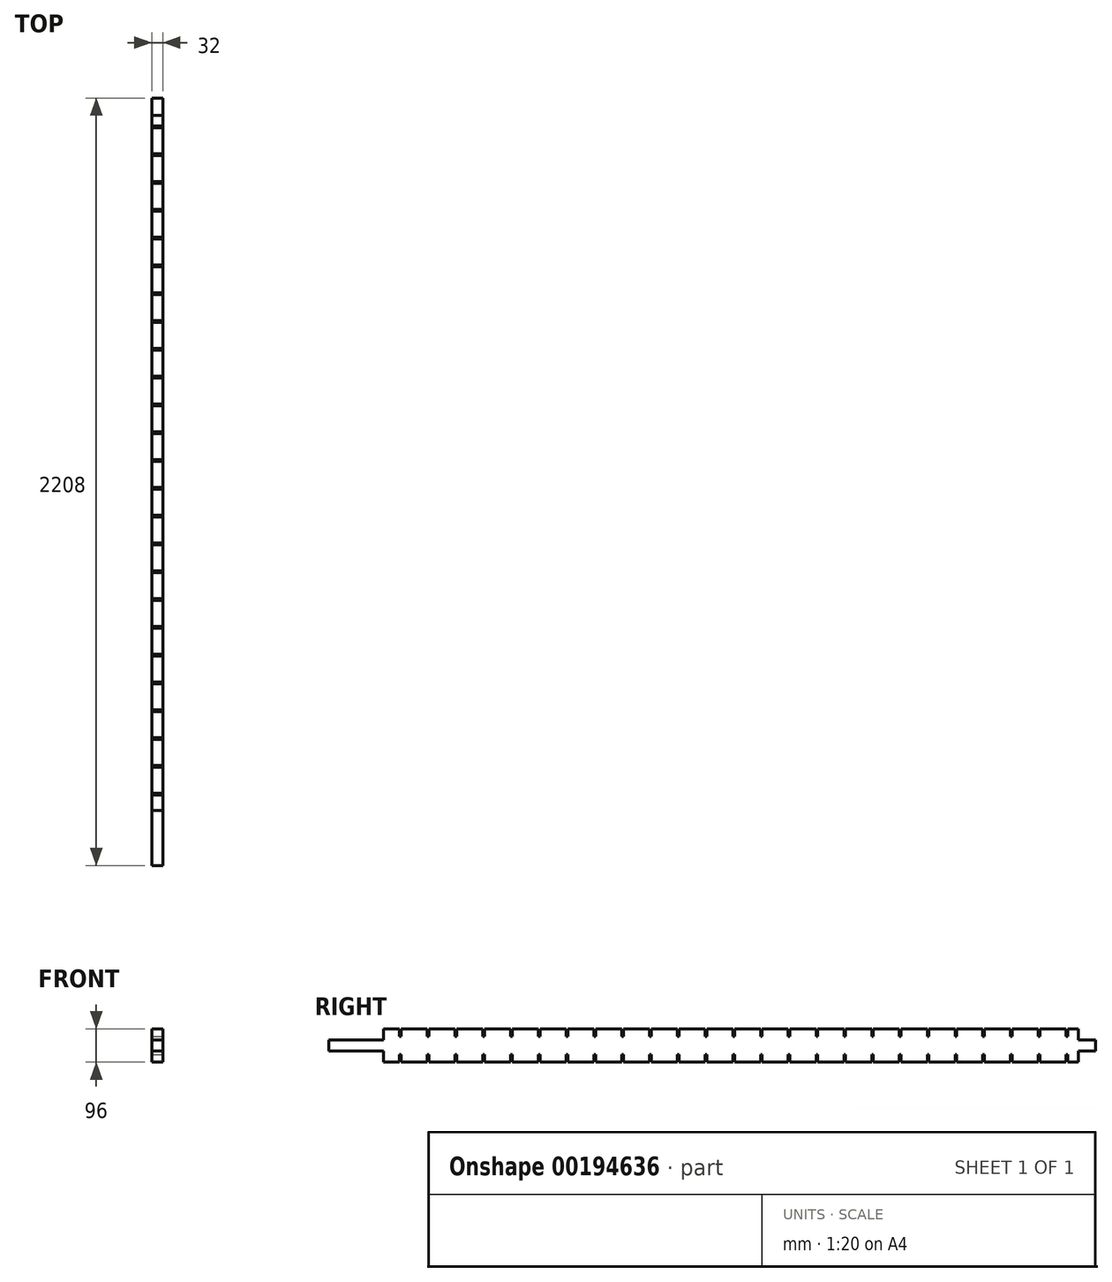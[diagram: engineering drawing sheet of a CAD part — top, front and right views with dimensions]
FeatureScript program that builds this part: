
annotation { "Feature Type Name" : "Feature", "Feature Type Description" : "" }
export const myFeature = defineFeature(function(context is Context, id is Id, definition is map)
    precondition{}
    {
        {
            var Q0;
            Q0=qCreatedBy(makeId("Front.planeOp"),FACE);
            var sketch = newSketch(context, id + "F0", { "sketchPlane" : qUnion([Q0])});
            skLineSegment(sketch, "E0.bottom", {"start": v(16, -16) * mm, "end": v(-16, -16) * mm});
            skLineSegment(sketch, "E0.top", {"start": v(16, 16) * mm, "end": v(-16, 16) * mm});
            skLineSegment(sketch, "E0.left", {"start": v(16, -16) * mm, "end": v(16, 16) * mm});
            skLineSegment(sketch, "E0.right", {"start": v(-16, -16) * mm, "end": v(-16, 16) * mm});
            skPoint(sketch, "E0.middle", {"position": v(0, 0) * mm});
            skSolve(sketch);
        }
        {
            var Q0;
            Q0 = qSketchRegion(id + "F0", true);
            extrude(context, id + "F1", {"entities" : qUnion([Q0]), "depth" : 2208 * mm});
        }
        {
            var Q0;
            Q0=qCreatedBy(makeId("Front.planeOp"),FACE);
            cPlane(context, id + "F2", {"entities" : qUnion([Q0]), "cplaneType" : CPlaneType.OFFSET, "offset" : 50 * mm, "width" : 150 * mm, "height" : 150 * mm});
        }
        {
            var Q0;
            Q0=qCreatedBy(id+"F2.planeOp",FACE);
            var sketch = newSketch(context, id + "F3", { "sketchPlane" : qUnion([Q0])});
            skLineSegment(sketch, "E1.bottom", {"start": v(16, 16) * mm, "end": v(-16, 16) * mm});
            skLineSegment(sketch, "E1.top", {"start": v(16, 48) * mm, "end": v(-16, 48) * mm});
            skLineSegment(sketch, "E1.left", {"start": v(16, 16) * mm, "end": v(16, 48) * mm});
            skLineSegment(sketch, "E1.right", {"start": v(-16, 16) * mm, "end": v(-16, 48) * mm});
            skPoint(sketch, "E1.middle", {"position": v(0, 32) * mm});
            skLineSegment(sketch, "E2.bottom", {"start": v(16, -16) * mm, "end": v(-16, -16) * mm});
            skLineSegment(sketch, "E2.top", {"start": v(16, -48) * mm, "end": v(-16, -48) * mm});
            skLineSegment(sketch, "E2.left", {"start": v(16, -16) * mm, "end": v(16, -48) * mm});
            skLineSegment(sketch, "E2.right", {"start": v(-16, -16) * mm, "end": v(-16, -48) * mm});
            skPoint(sketch, "E2.middle", {"position": v(0, -32) * mm});
            skSolve(sketch);
        }
        {
            var Q0;
            Q0 = qSketchRegion(id + "F3", true);
            extrude(context, id + "F4", {"entities" : qUnion([Q0]), "operationType" : NewBodyOperationType.ADD, "depth" : 2000 * mm});
        }
        {
            var Q0;
            Q0=makeQuery(id+"F4.boolean.opBoolean","MERGE",FACE,{"derivedFrom":[makeQuery(id+"F1.opExtrude","SWEPT_FACE",FACE,{"disambiguationData":[OSD([sQuery(id+"F0.wireOp",EDGE,"E0.left")])]}),makeQuery(id+"F4.opExtrude","SWEPT_FACE",FACE,{"disambiguationData":[OSD([sQuery(id+"F3.wireOp",EDGE,"E1.left")])]}),makeQuery(id+"F4.opExtrude","SWEPT_FACE",FACE,{"disambiguationData":[OSD([sQuery(id+"F3.wireOp",EDGE,"E2.left")])]})]});
            var sketch = newSketch(context, id + "F5", { "sketchPlane" : qUnion([Q0])});
            skLineSegment(sketch, "E3.0", {"start": v(-80, 26) * mm, "end": v(-80, 48) * mm});
            skLineSegment(sketch, "E4", {"start": v(-80, -48) * mm, "end": v(-85, -48) * mm});
            skLineSegment(sketch, "E5", {"start": v(-85, 48) * mm, "end": v(-85, 26) * mm});
            skLineSegment(sketch, "E6", {"start": v(-85, 26) * mm, "end": v(-80, 26) * mm});
            skLineSegment(sketch, "E7", {"start": v(-80, -26) * mm, "end": v(-80, -48) * mm});
            skLineSegment(sketch, "E8", {"start": v(-85, -26) * mm, "end": v(-80, -26) * mm});
            skLineSegment(sketch, "E9.trimOffspring", {"start": v(-85, -26) * mm, "end": v(-85, -48) * mm});
            skLineSegment(sketch, "E10", {"start": v(-85, 48) * mm, "end": v(-80, 48) * mm});
            skLineSegment(sketch, "E11.1.0.0", {"start": v(-160, 26) * mm, "end": v(-160, 48) * mm});
            skLineSegment(sketch, "E11.1.0.1", {"start": v(-165, 48) * mm, "end": v(-165, 26) * mm});
            skLineSegment(sketch, "E11.1.0.2", {"start": v(-165, 26) * mm, "end": v(-160, 26) * mm});
            skLineSegment(sketch, "E11.1.0.3", {"start": v(-160, -26) * mm, "end": v(-160, -48) * mm});
            skLineSegment(sketch, "E11.1.0.4", {"start": v(-165, -26) * mm, "end": v(-160, -26) * mm});
            skLineSegment(sketch, "E11.1.0.5", {"start": v(-165, -26) * mm, "end": v(-165, -48) * mm});
            skLineSegment(sketch, "E11.1.0.6", {"start": v(-165, 48) * mm, "end": v(-160, 48) * mm});
            skLineSegment(sketch, "E11.1.0.7", {"start": v(-160, -48) * mm, "end": v(-165, -48) * mm});
            skLineSegment(sketch, "E11.2.0.0", {"start": v(-240, 26) * mm, "end": v(-240, 48) * mm});
            skLineSegment(sketch, "E11.2.0.1", {"start": v(-245, 48) * mm, "end": v(-245, 26) * mm});
            skLineSegment(sketch, "E11.2.0.2", {"start": v(-245, 26) * mm, "end": v(-240, 26) * mm});
            skLineSegment(sketch, "E11.2.0.3", {"start": v(-240, -26) * mm, "end": v(-240, -48) * mm});
            skLineSegment(sketch, "E11.2.0.4", {"start": v(-245, -26) * mm, "end": v(-240, -26) * mm});
            skLineSegment(sketch, "E11.2.0.5", {"start": v(-245, -26) * mm, "end": v(-245, -48) * mm});
            skLineSegment(sketch, "E11.2.0.6", {"start": v(-245, 48) * mm, "end": v(-240, 48) * mm});
            skLineSegment(sketch, "E11.2.0.7", {"start": v(-240, -48) * mm, "end": v(-245, -48) * mm});
            skLineSegment(sketch, "E11.3.0.0", {"start": v(-320, 26) * mm, "end": v(-320, 48) * mm});
            skLineSegment(sketch, "E11.3.0.1", {"start": v(-325, 48) * mm, "end": v(-325, 26) * mm});
            skLineSegment(sketch, "E11.3.0.2", {"start": v(-325, 26) * mm, "end": v(-320, 26) * mm});
            skLineSegment(sketch, "E11.3.0.3", {"start": v(-320, -26) * mm, "end": v(-320, -48) * mm});
            skLineSegment(sketch, "E11.3.0.4", {"start": v(-325, -26) * mm, "end": v(-320, -26) * mm});
            skLineSegment(sketch, "E11.3.0.5", {"start": v(-325, -26) * mm, "end": v(-325, -48) * mm});
            skLineSegment(sketch, "E11.3.0.6", {"start": v(-325, 48) * mm, "end": v(-320, 48) * mm});
            skLineSegment(sketch, "E11.3.0.7", {"start": v(-320, -48) * mm, "end": v(-325, -48) * mm});
            skLineSegment(sketch, "E11.4.0.0", {"start": v(-400, 26) * mm, "end": v(-400, 48) * mm});
            skLineSegment(sketch, "E11.4.0.1", {"start": v(-405, 48) * mm, "end": v(-405, 26) * mm});
            skLineSegment(sketch, "E11.4.0.2", {"start": v(-405, 26) * mm, "end": v(-400, 26) * mm});
            skLineSegment(sketch, "E11.4.0.3", {"start": v(-400, -26) * mm, "end": v(-400, -48) * mm});
            skLineSegment(sketch, "E11.4.0.4", {"start": v(-405, -26) * mm, "end": v(-400, -26) * mm});
            skLineSegment(sketch, "E11.4.0.5", {"start": v(-405, -26) * mm, "end": v(-405, -48) * mm});
            skLineSegment(sketch, "E11.4.0.6", {"start": v(-405, 48) * mm, "end": v(-400, 48) * mm});
            skLineSegment(sketch, "E11.4.0.7", {"start": v(-400, -48) * mm, "end": v(-405, -48) * mm});
            skLineSegment(sketch, "E11.5.0.0", {"start": v(-480, 26) * mm, "end": v(-480, 48) * mm});
            skLineSegment(sketch, "E11.5.0.1", {"start": v(-485, 48) * mm, "end": v(-485, 26) * mm});
            skLineSegment(sketch, "E11.5.0.2", {"start": v(-485, 26) * mm, "end": v(-480, 26) * mm});
            skLineSegment(sketch, "E11.5.0.3", {"start": v(-480, -26) * mm, "end": v(-480, -48) * mm});
            skLineSegment(sketch, "E11.5.0.4", {"start": v(-485, -26) * mm, "end": v(-480, -26) * mm});
            skLineSegment(sketch, "E11.5.0.5", {"start": v(-485, -26) * mm, "end": v(-485, -48) * mm});
            skLineSegment(sketch, "E11.5.0.6", {"start": v(-485, 48) * mm, "end": v(-480, 48) * mm});
            skLineSegment(sketch, "E11.5.0.7", {"start": v(-480, -48) * mm, "end": v(-485, -48) * mm});
            skLineSegment(sketch, "E11.6.0.0", {"start": v(-560, 26) * mm, "end": v(-560, 48) * mm});
            skLineSegment(sketch, "E11.6.0.1", {"start": v(-565, 48) * mm, "end": v(-565, 26) * mm});
            skLineSegment(sketch, "E11.6.0.2", {"start": v(-565, 26) * mm, "end": v(-560, 26) * mm});
            skLineSegment(sketch, "E11.6.0.3", {"start": v(-560, -26) * mm, "end": v(-560, -48) * mm});
            skLineSegment(sketch, "E11.6.0.4", {"start": v(-565, -26) * mm, "end": v(-560, -26) * mm});
            skLineSegment(sketch, "E11.6.0.5", {"start": v(-565, -26) * mm, "end": v(-565, -48) * mm});
            skLineSegment(sketch, "E11.6.0.6", {"start": v(-565, 48) * mm, "end": v(-560, 48) * mm});
            skLineSegment(sketch, "E11.6.0.7", {"start": v(-560, -48) * mm, "end": v(-565, -48) * mm});
            skLineSegment(sketch, "E11.7.0.0", {"start": v(-640, 26) * mm, "end": v(-640, 48) * mm});
            skLineSegment(sketch, "E11.7.0.1", {"start": v(-645, 48) * mm, "end": v(-645, 26) * mm});
            skLineSegment(sketch, "E11.7.0.2", {"start": v(-645, 26) * mm, "end": v(-640, 26) * mm});
            skLineSegment(sketch, "E11.7.0.3", {"start": v(-640, -26) * mm, "end": v(-640, -48) * mm});
            skLineSegment(sketch, "E11.7.0.4", {"start": v(-645, -26) * mm, "end": v(-640, -26) * mm});
            skLineSegment(sketch, "E11.7.0.5", {"start": v(-645, -26) * mm, "end": v(-645, -48) * mm});
            skLineSegment(sketch, "E11.7.0.6", {"start": v(-645, 48) * mm, "end": v(-640, 48) * mm});
            skLineSegment(sketch, "E11.7.0.7", {"start": v(-640, -48) * mm, "end": v(-645, -48) * mm});
            skLineSegment(sketch, "E11.8.0.0", {"start": v(-720, 26) * mm, "end": v(-720, 48) * mm});
            skLineSegment(sketch, "E11.8.0.1", {"start": v(-725, 48) * mm, "end": v(-725, 26) * mm});
            skLineSegment(sketch, "E11.8.0.2", {"start": v(-725, 26) * mm, "end": v(-720, 26) * mm});
            skLineSegment(sketch, "E11.8.0.3", {"start": v(-720, -26) * mm, "end": v(-720, -48) * mm});
            skLineSegment(sketch, "E11.8.0.4", {"start": v(-725, -26) * mm, "end": v(-720, -26) * mm});
            skLineSegment(sketch, "E11.8.0.5", {"start": v(-725, -26) * mm, "end": v(-725, -48) * mm});
            skLineSegment(sketch, "E11.8.0.6", {"start": v(-725, 48) * mm, "end": v(-720, 48) * mm});
            skLineSegment(sketch, "E11.8.0.7", {"start": v(-720, -48) * mm, "end": v(-725, -48) * mm});
            skLineSegment(sketch, "E11.9.0.0", {"start": v(-800, 26) * mm, "end": v(-800, 48) * mm});
            skLineSegment(sketch, "E11.9.0.1", {"start": v(-805, 48) * mm, "end": v(-805, 26) * mm});
            skLineSegment(sketch, "E11.9.0.2", {"start": v(-805, 26) * mm, "end": v(-800, 26) * mm});
            skLineSegment(sketch, "E11.9.0.3", {"start": v(-800, -26) * mm, "end": v(-800, -48) * mm});
            skLineSegment(sketch, "E11.9.0.4", {"start": v(-805, -26) * mm, "end": v(-800, -26) * mm});
            skLineSegment(sketch, "E11.9.0.5", {"start": v(-805, -26) * mm, "end": v(-805, -48) * mm});
            skLineSegment(sketch, "E11.9.0.6", {"start": v(-805, 48) * mm, "end": v(-800, 48) * mm});
            skLineSegment(sketch, "E11.9.0.7", {"start": v(-800, -48) * mm, "end": v(-805, -48) * mm});
            skLineSegment(sketch, "E11.10.0.0", {"start": v(-880, 26) * mm, "end": v(-880, 48) * mm});
            skLineSegment(sketch, "E11.10.0.1", {"start": v(-885, 48) * mm, "end": v(-885, 26) * mm});
            skLineSegment(sketch, "E11.10.0.2", {"start": v(-885, 26) * mm, "end": v(-880, 26) * mm});
            skLineSegment(sketch, "E11.10.0.3", {"start": v(-880, -26) * mm, "end": v(-880, -48) * mm});
            skLineSegment(sketch, "E11.10.0.4", {"start": v(-885, -26) * mm, "end": v(-880, -26) * mm});
            skLineSegment(sketch, "E11.10.0.5", {"start": v(-885, -26) * mm, "end": v(-885, -48) * mm});
            skLineSegment(sketch, "E11.10.0.6", {"start": v(-885, 48) * mm, "end": v(-880, 48) * mm});
            skLineSegment(sketch, "E11.10.0.7", {"start": v(-880, -48) * mm, "end": v(-885, -48) * mm});
            skLineSegment(sketch, "E11.11.0.0", {"start": v(-960, 26) * mm, "end": v(-960, 48) * mm});
            skLineSegment(sketch, "E11.11.0.1", {"start": v(-965, 48) * mm, "end": v(-965, 26) * mm});
            skLineSegment(sketch, "E11.11.0.2", {"start": v(-965, 26) * mm, "end": v(-960, 26) * mm});
            skLineSegment(sketch, "E11.11.0.3", {"start": v(-960, -26) * mm, "end": v(-960, -48) * mm});
            skLineSegment(sketch, "E11.11.0.4", {"start": v(-965, -26) * mm, "end": v(-960, -26) * mm});
            skLineSegment(sketch, "E11.11.0.5", {"start": v(-965, -26) * mm, "end": v(-965, -48) * mm});
            skLineSegment(sketch, "E11.11.0.6", {"start": v(-965, 48) * mm, "end": v(-960, 48) * mm});
            skLineSegment(sketch, "E11.11.0.7", {"start": v(-960, -48) * mm, "end": v(-965, -48) * mm});
            skLineSegment(sketch, "E11.12.0.0", {"start": v(-1040, 26) * mm, "end": v(-1040, 48) * mm});
            skLineSegment(sketch, "E11.12.0.1", {"start": v(-1045, 48) * mm, "end": v(-1045, 26) * mm});
            skLineSegment(sketch, "E11.12.0.2", {"start": v(-1045, 26) * mm, "end": v(-1040, 26) * mm});
            skLineSegment(sketch, "E11.12.0.3", {"start": v(-1040, -26) * mm, "end": v(-1040, -48) * mm});
            skLineSegment(sketch, "E11.12.0.4", {"start": v(-1045, -26) * mm, "end": v(-1040, -26) * mm});
            skLineSegment(sketch, "E11.12.0.5", {"start": v(-1045, -26) * mm, "end": v(-1045, -48) * mm});
            skLineSegment(sketch, "E11.12.0.6", {"start": v(-1045, 48) * mm, "end": v(-1040, 48) * mm});
            skLineSegment(sketch, "E11.12.0.7", {"start": v(-1040, -48) * mm, "end": v(-1045, -48) * mm});
            skLineSegment(sketch, "E11.13.0.0", {"start": v(-1120, 26) * mm, "end": v(-1120, 48) * mm});
            skLineSegment(sketch, "E11.13.0.1", {"start": v(-1125, 48) * mm, "end": v(-1125, 26) * mm});
            skLineSegment(sketch, "E11.13.0.2", {"start": v(-1125, 26) * mm, "end": v(-1120, 26) * mm});
            skLineSegment(sketch, "E11.13.0.3", {"start": v(-1120, -26) * mm, "end": v(-1120, -48) * mm});
            skLineSegment(sketch, "E11.13.0.4", {"start": v(-1125, -26) * mm, "end": v(-1120, -26) * mm});
            skLineSegment(sketch, "E11.13.0.5", {"start": v(-1125, -26) * mm, "end": v(-1125, -48) * mm});
            skLineSegment(sketch, "E11.13.0.6", {"start": v(-1125, 48) * mm, "end": v(-1120, 48) * mm});
            skLineSegment(sketch, "E11.13.0.7", {"start": v(-1120, -48) * mm, "end": v(-1125, -48) * mm});
            skLineSegment(sketch, "E11.14.0.0", {"start": v(-1200, 26) * mm, "end": v(-1200, 48) * mm});
            skLineSegment(sketch, "E11.14.0.1", {"start": v(-1205, 48) * mm, "end": v(-1205, 26) * mm});
            skLineSegment(sketch, "E11.14.0.2", {"start": v(-1205, 26) * mm, "end": v(-1200, 26) * mm});
            skLineSegment(sketch, "E11.14.0.3", {"start": v(-1200, -26) * mm, "end": v(-1200, -48) * mm});
            skLineSegment(sketch, "E11.14.0.4", {"start": v(-1205, -26) * mm, "end": v(-1200, -26) * mm});
            skLineSegment(sketch, "E11.14.0.5", {"start": v(-1205, -26) * mm, "end": v(-1205, -48) * mm});
            skLineSegment(sketch, "E11.14.0.6", {"start": v(-1205, 48) * mm, "end": v(-1200, 48) * mm});
            skLineSegment(sketch, "E11.14.0.7", {"start": v(-1200, -48) * mm, "end": v(-1205, -48) * mm});
            skLineSegment(sketch, "E11.direction1", {"start": v(-85, -48) * mm, "end": v(-165, -48) * mm, "construction": true});
            skLineSegment(sketch, "E12.0.15.0", {"start": v(-1280, 26) * mm, "end": v(-1280, 48) * mm});
            skLineSegment(sketch, "E12.3.15.0", {"start": v(-1285, 48) * mm, "end": v(-1285, 26) * mm});
            skLineSegment(sketch, "E12.6.15.0", {"start": v(-1285, 26) * mm, "end": v(-1280, 26) * mm});
            skLineSegment(sketch, "E12.9.15.0", {"start": v(-1280, -26) * mm, "end": v(-1280, -48) * mm});
            skLineSegment(sketch, "E12.12.15.0", {"start": v(-1285, -26) * mm, "end": v(-1280, -26) * mm});
            skLineSegment(sketch, "E12.15.15.0", {"start": v(-1285, -26) * mm, "end": v(-1285, -48) * mm});
            skLineSegment(sketch, "E12.18.15.0", {"start": v(-1285, 48) * mm, "end": v(-1280, 48) * mm});
            skLineSegment(sketch, "E12.21.15.0", {"start": v(-1280, -48) * mm, "end": v(-1285, -48) * mm});
            skLineSegment(sketch, "E12.0.16.0", {"start": v(-1360, 26) * mm, "end": v(-1360, 48) * mm});
            skLineSegment(sketch, "E12.3.16.0", {"start": v(-1365, 48) * mm, "end": v(-1365, 26) * mm});
            skLineSegment(sketch, "E12.6.16.0", {"start": v(-1365, 26) * mm, "end": v(-1360, 26) * mm});
            skLineSegment(sketch, "E12.9.16.0", {"start": v(-1360, -26) * mm, "end": v(-1360, -48) * mm});
            skLineSegment(sketch, "E12.12.16.0", {"start": v(-1365, -26) * mm, "end": v(-1360, -26) * mm});
            skLineSegment(sketch, "E12.15.16.0", {"start": v(-1365, -26) * mm, "end": v(-1365, -48) * mm});
            skLineSegment(sketch, "E12.18.16.0", {"start": v(-1365, 48) * mm, "end": v(-1360, 48) * mm});
            skLineSegment(sketch, "E12.21.16.0", {"start": v(-1360, -48) * mm, "end": v(-1365, -48) * mm});
            skLineSegment(sketch, "E12.0.17.0", {"start": v(-1440, 26) * mm, "end": v(-1440, 48) * mm});
            skLineSegment(sketch, "E12.3.17.0", {"start": v(-1445, 48) * mm, "end": v(-1445, 26) * mm});
            skLineSegment(sketch, "E12.6.17.0", {"start": v(-1445, 26) * mm, "end": v(-1440, 26) * mm});
            skLineSegment(sketch, "E12.9.17.0", {"start": v(-1440, -26) * mm, "end": v(-1440, -48) * mm});
            skLineSegment(sketch, "E12.12.17.0", {"start": v(-1445, -26) * mm, "end": v(-1440, -26) * mm});
            skLineSegment(sketch, "E12.15.17.0", {"start": v(-1445, -26) * mm, "end": v(-1445, -48) * mm});
            skLineSegment(sketch, "E12.18.17.0", {"start": v(-1445, 48) * mm, "end": v(-1440, 48) * mm});
            skLineSegment(sketch, "E12.21.17.0", {"start": v(-1440, -48) * mm, "end": v(-1445, -48) * mm});
            skLineSegment(sketch, "E12.0.18.0", {"start": v(-1520, 26) * mm, "end": v(-1520, 48) * mm});
            skLineSegment(sketch, "E12.3.18.0", {"start": v(-1525, 48) * mm, "end": v(-1525, 26) * mm});
            skLineSegment(sketch, "E12.6.18.0", {"start": v(-1525, 26) * mm, "end": v(-1520, 26) * mm});
            skLineSegment(sketch, "E12.9.18.0", {"start": v(-1520, -26) * mm, "end": v(-1520, -48) * mm});
            skLineSegment(sketch, "E12.12.18.0", {"start": v(-1525, -26) * mm, "end": v(-1520, -26) * mm});
            skLineSegment(sketch, "E12.15.18.0", {"start": v(-1525, -26) * mm, "end": v(-1525, -48) * mm});
            skLineSegment(sketch, "E12.18.18.0", {"start": v(-1525, 48) * mm, "end": v(-1520, 48) * mm});
            skLineSegment(sketch, "E12.21.18.0", {"start": v(-1520, -48) * mm, "end": v(-1525, -48) * mm});
            skLineSegment(sketch, "E12.0.19.0", {"start": v(-1600, 26) * mm, "end": v(-1600, 48) * mm});
            skLineSegment(sketch, "E12.3.19.0", {"start": v(-1605, 48) * mm, "end": v(-1605, 26) * mm});
            skLineSegment(sketch, "E12.6.19.0", {"start": v(-1605, 26) * mm, "end": v(-1600, 26) * mm});
            skLineSegment(sketch, "E12.9.19.0", {"start": v(-1600, -26) * mm, "end": v(-1600, -48) * mm});
            skLineSegment(sketch, "E12.12.19.0", {"start": v(-1605, -26) * mm, "end": v(-1600, -26) * mm});
            skLineSegment(sketch, "E12.15.19.0", {"start": v(-1605, -26) * mm, "end": v(-1605, -48) * mm});
            skLineSegment(sketch, "E12.18.19.0", {"start": v(-1605, 48) * mm, "end": v(-1600, 48) * mm});
            skLineSegment(sketch, "E12.21.19.0", {"start": v(-1600, -48) * mm, "end": v(-1605, -48) * mm});
            skLineSegment(sketch, "E12.0.20.0", {"start": v(-1680, 26) * mm, "end": v(-1680, 48) * mm});
            skLineSegment(sketch, "E12.3.20.0", {"start": v(-1685, 48) * mm, "end": v(-1685, 26) * mm});
            skLineSegment(sketch, "E12.6.20.0", {"start": v(-1685, 26) * mm, "end": v(-1680, 26) * mm});
            skLineSegment(sketch, "E12.9.20.0", {"start": v(-1680, -26) * mm, "end": v(-1680, -48) * mm});
            skLineSegment(sketch, "E12.12.20.0", {"start": v(-1685, -26) * mm, "end": v(-1680, -26) * mm});
            skLineSegment(sketch, "E12.15.20.0", {"start": v(-1685, -26) * mm, "end": v(-1685, -48) * mm});
            skLineSegment(sketch, "E12.18.20.0", {"start": v(-1685, 48) * mm, "end": v(-1680, 48) * mm});
            skLineSegment(sketch, "E12.21.20.0", {"start": v(-1680, -48) * mm, "end": v(-1685, -48) * mm});
            skLineSegment(sketch, "E12.0.21.0", {"start": v(-1760, 26) * mm, "end": v(-1760, 48) * mm});
            skLineSegment(sketch, "E12.3.21.0", {"start": v(-1765, 48) * mm, "end": v(-1765, 26) * mm});
            skLineSegment(sketch, "E12.6.21.0", {"start": v(-1765, 26) * mm, "end": v(-1760, 26) * mm});
            skLineSegment(sketch, "E12.9.21.0", {"start": v(-1760, -26) * mm, "end": v(-1760, -48) * mm});
            skLineSegment(sketch, "E12.12.21.0", {"start": v(-1765, -26) * mm, "end": v(-1760, -26) * mm});
            skLineSegment(sketch, "E12.15.21.0", {"start": v(-1765, -26) * mm, "end": v(-1765, -48) * mm});
            skLineSegment(sketch, "E12.18.21.0", {"start": v(-1765, 48) * mm, "end": v(-1760, 48) * mm});
            skLineSegment(sketch, "E12.21.21.0", {"start": v(-1760, -48) * mm, "end": v(-1765, -48) * mm});
            skLineSegment(sketch, "E12.0.22.0", {"start": v(-1840, 26) * mm, "end": v(-1840, 48) * mm});
            skLineSegment(sketch, "E12.3.22.0", {"start": v(-1845, 48) * mm, "end": v(-1845, 26) * mm});
            skLineSegment(sketch, "E12.6.22.0", {"start": v(-1845, 26) * mm, "end": v(-1840, 26) * mm});
            skLineSegment(sketch, "E12.9.22.0", {"start": v(-1840, -26) * mm, "end": v(-1840, -48) * mm});
            skLineSegment(sketch, "E12.12.22.0", {"start": v(-1845, -26) * mm, "end": v(-1840, -26) * mm});
            skLineSegment(sketch, "E12.15.22.0", {"start": v(-1845, -26) * mm, "end": v(-1845, -48) * mm});
            skLineSegment(sketch, "E12.18.22.0", {"start": v(-1845, 48) * mm, "end": v(-1840, 48) * mm});
            skLineSegment(sketch, "E12.21.22.0", {"start": v(-1840, -48) * mm, "end": v(-1845, -48) * mm});
            skLineSegment(sketch, "E12.0.23.0", {"start": v(-1920, 26) * mm, "end": v(-1920, 48) * mm});
            skLineSegment(sketch, "E12.3.23.0", {"start": v(-1925, 48) * mm, "end": v(-1925, 26) * mm});
            skLineSegment(sketch, "E12.6.23.0", {"start": v(-1925, 26) * mm, "end": v(-1920, 26) * mm});
            skLineSegment(sketch, "E12.9.23.0", {"start": v(-1920, -26) * mm, "end": v(-1920, -48) * mm});
            skLineSegment(sketch, "E12.12.23.0", {"start": v(-1925, -26) * mm, "end": v(-1920, -26) * mm});
            skLineSegment(sketch, "E12.15.23.0", {"start": v(-1925, -26) * mm, "end": v(-1925, -48) * mm});
            skLineSegment(sketch, "E12.18.23.0", {"start": v(-1925, 48) * mm, "end": v(-1920, 48) * mm});
            skLineSegment(sketch, "E12.21.23.0", {"start": v(-1920, -48) * mm, "end": v(-1925, -48) * mm});
            skLineSegment(sketch, "E12.0.24.0", {"start": v(-2000, 26) * mm, "end": v(-2000, 48) * mm});
            skLineSegment(sketch, "E12.3.24.0", {"start": v(-2005, 48) * mm, "end": v(-2005, 26) * mm});
            skLineSegment(sketch, "E12.6.24.0", {"start": v(-2005, 26) * mm, "end": v(-2000, 26) * mm});
            skLineSegment(sketch, "E12.9.24.0", {"start": v(-2000, -26) * mm, "end": v(-2000, -48) * mm});
            skLineSegment(sketch, "E12.12.24.0", {"start": v(-2005, -26) * mm, "end": v(-2000, -26) * mm});
            skLineSegment(sketch, "E12.15.24.0", {"start": v(-2005, -26) * mm, "end": v(-2005, -48) * mm});
            skLineSegment(sketch, "E12.18.24.0", {"start": v(-2005, 48) * mm, "end": v(-2000, 48) * mm});
            skLineSegment(sketch, "E12.21.24.0", {"start": v(-2000, -48) * mm, "end": v(-2005, -48) * mm});
            skSolve(sketch);
        }
        {
            var Q0;
            Q0 = qSketchRegion(id + "F5", true);
            extrude(context, id + "F6", {"entities" : qUnion([Q0]), "operationType" : NewBodyOperationType.REMOVE, "oppositeDirection" : true, "depth" : 32 * mm});
        }
    });
